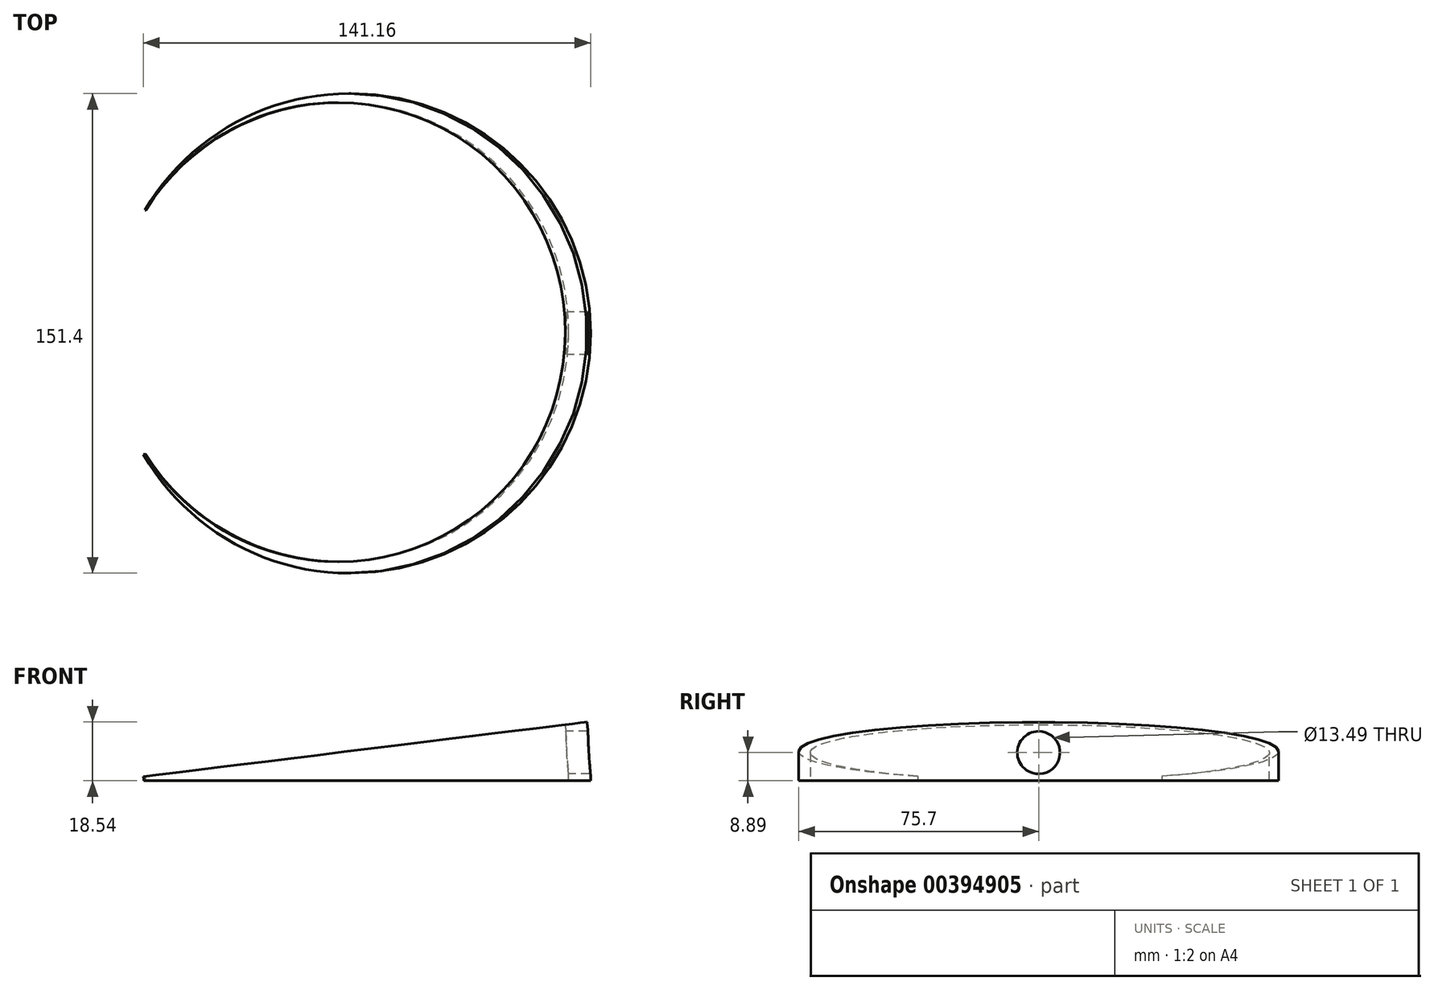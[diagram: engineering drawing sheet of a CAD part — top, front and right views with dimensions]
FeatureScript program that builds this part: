
annotation { "Feature Type Name" : "Feature", "Feature Type Description" : "" }
export const myFeature = defineFeature(function(context is Context, id is Id, definition is map)
    precondition{}
    {
        {
            var Q0;
            Q0=qCreatedBy(makeId("Top.planeOp"),FACE);
            var sketch = newSketch(context, id + "F0", { "sketchPlane" : qUnion([Q0])});
            skArc(sketch, "E0", {"start": v(0, -75.7) * mm, "mid": v(75.7, 0) * mm, "end": v(0, 75.7) * mm});
            skLineSegment(sketch, "E1", {"start": v(-76.44, 0) * mm, "end": v(-76.44, -31.39) * mm});
            skArc(sketch, "E2", {"start": v(-65.38, -38.16) * mm, "mid": v(75.7, -0.44) * mm, "end": v(-64.92, 38.93) * mm});
            skArc(sketch, "E3", {"start": v(68.76, 0) * mm, "mid": v(16.76, 69.98) * mm, "end": v(-64.72, 38.93) * mm});
            skArc(sketch, "E4", {"start": v(-64.72, -38.16) * mm, "mid": v(16.39, -69.32) * mm, "end": v(68.76, 0) * mm});
            skLineSegment(sketch, "E5", {"start": v(-64.72, -38.16) * mm, "end": v(-65.38, -38.16) * mm});
            skLineSegment(sketch, "E6", {"start": v(-64.72, 38.93) * mm, "end": v(-64.92, 38.93) * mm});
            skPoint(sketch, "E7.orphan", {"position": v(-75.7, 0) * mm});
            skSolve(sketch);
        }
        {
            var Q0;
            Q0 = qSketchRegion(id + "F0", true);
            var Q1;
            Q1=sQuery(id+"F0.wireOp",EDGE,"E1");
            revolve(context, id + "F1", {"entities" : qUnion([Q0]), "axis" : qUnion([Q1]), "revolveType" : RevolveType.ONE_DIRECTION, "angle" : 7 * degree});
        }
        {
            var Q0;
            Q0=qCreatedBy(makeId("Right.planeOp"),FACE);
            var sketch = newSketch(context, id + "F2", { "sketchPlane" : qUnion([Q0])});
            skCircle(sketch, "E8", {"center": v(0, 8.9) * mm, "radius": 6.74 * mm});
            skSolve(sketch);
        }
        {
            var Q0;
            Q0=qSketchRegion(id+"F2",true);
            extrude(context, id + "F3", {"entities" : qUnion([Q0]), "operationType" : NewBodyOperationType.REMOVE, "depth" : 101.6 * mm});
        }
    });
